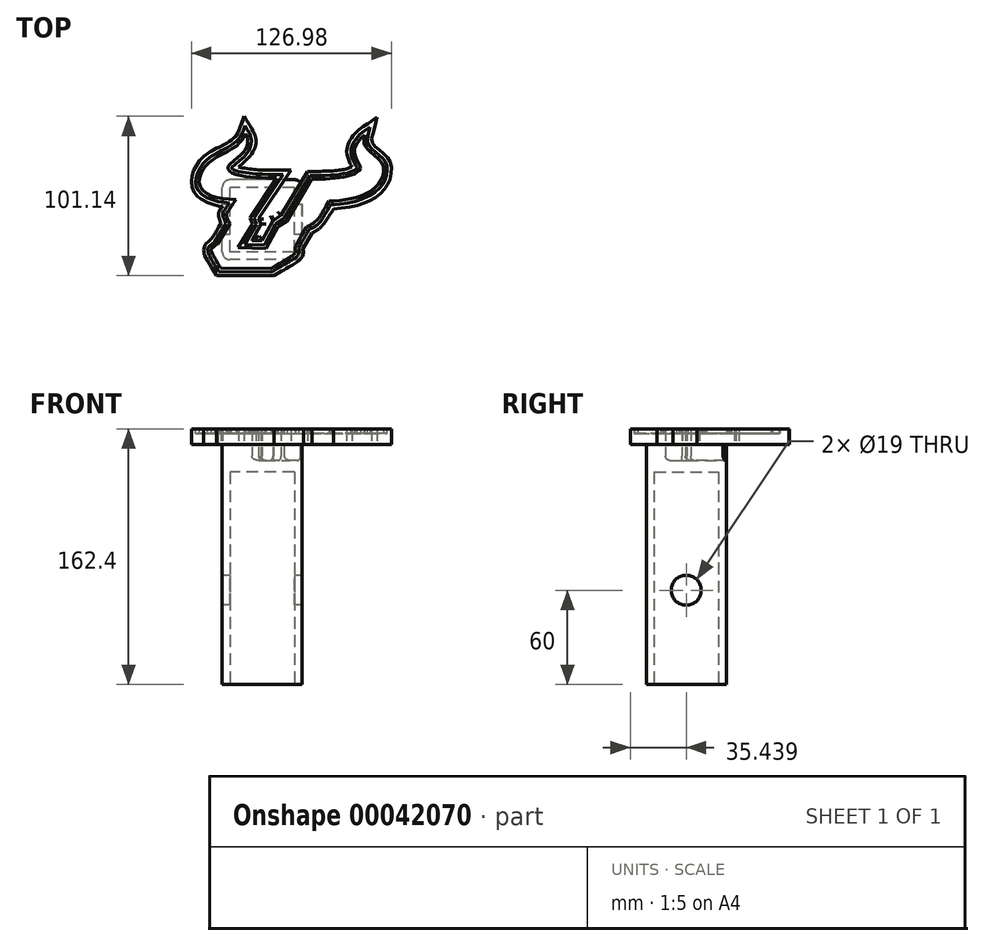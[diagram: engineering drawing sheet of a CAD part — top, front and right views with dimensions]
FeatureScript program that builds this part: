
annotation { "Feature Type Name" : "Feature", "Feature Type Description" : "" }
export const myFeature = defineFeature(function(context is Context, id is Id, definition is map)
    precondition{}
    {
        {
            var Q0;
            Q0=qCreatedBy(makeId("Top.planeOp"),FACE);
            var sketch = newSketch(context, id + "F0", { "sketchPlane" : qUnion([Q0])});
            skFitSpline(sketch, "E0", {"points": [v(-30.7, 0) * mm, v(-32.33, -4.67) * mm, v(-34.46, -10.08) * mm, v(-36.43, -13.03) * mm, v(-39.21, -15.48) * mm, v(-46.09, -19.42) * mm, v(-51.33, -22.04) * mm, v(-57.23, -26.46) * mm, v(-60.67, -30.72) * mm, v(-63.29, -35.96) * mm, v(-64.1, -40.87) * mm, v(-63.62, -45.62) * mm, v(-61.32, -50.04) * mm, v(-57.55, -53) * mm, v(-51.82, -55.45) * mm, v(-46.9, -56.92) * mm, v(-44.45, -57.42) * mm], "startDerivative": vector(-25.69, -73.33) * mm, "endDerivative": vector(51.93, -9.1) * mm});
            skFitSpline(sketch, "E1", {"points": [v(-45.41, -67.95) * mm, v(-46.66, -64.45) * mm, v(-46.9, -62.2) * mm, v(-46.48, -60.18) * mm, v(-44.45, -57.42) * mm], "startDerivative": vector(-5.18, 12.79) * mm, "endDerivative": vector(8.81, 10.21) * mm});
            skFitSpline(sketch, "E2", {"points": [v(-45.41, -67.95) * mm, v(-51.3, -77.63) * mm, v(-52.36, -78.64) * mm, v(-54.44, -80.66) * mm, v(-55.39, -81.67) * mm, v(-56.1, -83.15) * mm, v(-56.28, -86.06) * mm, v(-55.27, -89.44) * mm, v(-48.15, -101.14) * mm], "startDerivative": vector(-33.88, -59.15) * mm, "endDerivative": vector(37.77, -58.28) * mm});
            skFitSpline(sketch, "E3", {"points": [v(-48.15, -101.14) * mm, v(-11.53, -101.14) * mm], "startDerivative": vector(36.62, 0) * mm, "endDerivative": vector(36.62, 0) * mm});
            skFitSpline(sketch, "E4", {"points": [v(-11.53, -101.14) * mm, v(0.85, -93.86) * mm, v(4.9, -90.92) * mm, v(6.8, -87.77) * mm, v(6.74, -84.18) * mm], "startDerivative": vector(36.38, 21.09) * mm, "endDerivative": vector(-2.56, 19.04) * mm});
            skFitSpline(sketch, "E5", {"points": [v(6.74, -84.18) * mm, v(12.58, -74.1) * mm], "startDerivative": vector(5.84, 10.08) * mm, "endDerivative": vector(5.84, 10.08) * mm});
            skFitSpline(sketch, "E6", {"points": [v(12.58, -74.1) * mm, v(15.58, -72.35) * mm, v(19.02, -69.4) * mm, v(26.06, -58.87) * mm], "startDerivative": vector(12.25, 6.8) * mm, "endDerivative": vector(15.82, 25.96) * mm});
            skFitSpline(sketch, "E7", {"points": [v(26.06, -58.87) * mm, v(33, -58.08) * mm, v(33.75, -58.03) * mm, v(39.94, -56.83) * mm, v(48.02, -54.03) * mm, v(53.66, -50.94) * mm, v(57.86, -47.04) * mm, v(60.7, -42.9) * mm, v(62.45, -37.86) * mm, v(62.7, -31.22) * mm, v(61.2, -27.28) * mm, v(58.11, -23.73) * mm, v(53.82, -20.4) * mm, v(51.77, -18.3) * mm, v(50.38, -15.15) * mm, v(51.02, -11.6) * mm, v(53.82, -0.42) * mm], "startDerivative": vector(123.14, 15.03) * mm, "endDerivative": vector(32.52, 137.34) * mm});
            skFitSpline(sketch, "E8", {"points": [v(53.82, -0.42) * mm, v(46.53, -5.52) * mm, v(42.94, -8.11) * mm, v(39.04, -11.66) * mm, v(36.45, -15.5) * mm, v(34.95, -18.94) * mm, v(34.55, -23.34) * mm, v(36.35, -29.57) * mm, v(37.9, -32.12) * mm], "startDerivative": vector(-47.84, -33.44) * mm, "endDerivative": vector(15.88, -22.17) * mm});
            skFitSpline(sketch, "E9", {"points": [v(37.9, -32.12) * mm, v(35.85, -32.97) * mm, v(31.8, -33.97) * mm, v(26.41, -34.62) * mm, v(16.63, -35.02) * mm, v(9.44, -35.12) * mm], "startDerivative": vector(-14.51, -6.75) * mm, "endDerivative": vector(-29.29, -0.26) * mm});
            skFitSpline(sketch, "E10", {"points": [v(9.44, -35.12) * mm, v(-7.16, -62.85) * mm], "startDerivative": vector(-16.6, -27.73) * mm, "endDerivative": vector(-16.6, -27.73) * mm});
            skFitSpline(sketch, "E11", {"points": [v(-7.16, -62.85) * mm, v(-11.95, -66.25) * mm], "startDerivative": vector(-4.8, -3.4) * mm, "endDerivative": vector(-4.8, -3.4) * mm});
            skFitSpline(sketch, "E12", {"points": [v(-11.95, -66.25) * mm, v(-12.39, -66.25) * mm], "startDerivative": vector(-0.44, 0) * mm, "endDerivative": vector(-0.44, 0) * mm});
            skFitSpline(sketch, "E13", {"points": [v(-19.16, -78.81) * mm, v(-25.82, -78.81) * mm], "startDerivative": vector(-6.66, 0) * mm, "endDerivative": vector(-6.66, 0) * mm});
            skFitSpline(sketch, "E14", {"points": [v(-25.82, -78.81) * mm, v(-19.95, -68.31) * mm], "startDerivative": vector(5.86, 10.5) * mm, "endDerivative": vector(5.86, 10.5) * mm});
            skFitSpline(sketch, "E15", {"points": [v(-19.95, -68.31) * mm, v(-21.38, -65.1) * mm], "startDerivative": vector(-1.43, 3.2) * mm, "endDerivative": vector(-1.43, 3.2) * mm});
            skFitSpline(sketch, "E16", {"points": [v(-21.38, -65.1) * mm, v(-0.87, -34.23) * mm], "startDerivative": vector(20.5, 30.87) * mm, "endDerivative": vector(20.5, 30.87) * mm});
            skFitSpline(sketch, "E17", {"points": [v(-0.87, -34.23) * mm, v(-12.32, -34.23) * mm, v(-23.7, -33.86) * mm, v(-34.36, -32.32) * mm], "startDerivative": vector(-33.9, -0.05) * mm, "endDerivative": vector(-32.28, 5.6) * mm});
            skFitSpline(sketch, "E18", {"points": [v(-34.36, -32.32) * mm, v(-30.27, -28.8) * mm, v(-26.07, -24.04) * mm, v(-23.78, -19.68) * mm, v(-23.14, -16.55) * mm, v(-23.58, -13.02) * mm, v(-25.52, -8.55) * mm, v(-30.7, 0) * mm], "startDerivative": vector(28.11, 23.08) * mm, "endDerivative": vector(-29.43, 46.8) * mm});
            skLineSegment(sketch, "E19", {"start": v(-19.16, -78.81) * mm, "end": v(-12.39, -66.25) * mm});
            skFitSpline(sketch, "E20", {"points": [v(-29.86, -11) * mm, v(-30.67, -12.93) * mm, v(-31.74, -14.72) * mm, v(-33.53, -16.91) * mm, v(-36.44, -19.42) * mm, v(-40.83, -22.1) * mm, v(-45.3, -24.48) * mm, v(-50.46, -27.39) * mm, v(-53.41, -29.76) * mm, v(-55.83, -32.36) * mm, v(-57.76, -35.85) * mm, v(-58.97, -39.66) * mm, v(-59.01, -43.15) * mm, v(-57.44, -46.55) * mm, v(-54.09, -49.24) * mm, v(-49.43, -51.25) * mm, v(-44.06, -52.33) * mm, v(-35.96, -53) * mm], "startDerivative": vector(-18.17, -47.16) * mm, "endDerivative": vector(103.54, -6.88) * mm});
            skFitSpline(sketch, "E21", {"points": [v(-35.96, -53) * mm, v(-41.07, -60.57) * mm, v(-41.71, -61.5) * mm, v(-41.91, -61.86) * mm, v(-42, -62.29) * mm, v(-41.91, -63.1) * mm, v(-41.3, -65) * mm, v(-39.71, -68.27) * mm], "startDerivative": vector(-19.95, -29.75) * mm, "endDerivative": vector(8.84, -17.26) * mm});
            skFitSpline(sketch, "E22", {"points": [v(-39.71, -68.27) * mm, v(-47.67, -81.04) * mm], "startDerivative": vector(-7.95, -12.78) * mm, "endDerivative": vector(-7.95, -12.78) * mm});
            skFitSpline(sketch, "E23", {"points": [v(-47.67, -81.04) * mm, v(-50.91, -83.72) * mm, v(-51.33, -84.14) * mm, v(-51.56, -84.85) * mm, v(-51.17, -86.51) * mm, v(-45.64, -96.33) * mm], "startDerivative": vector(-16.29, -13.47) * mm, "endDerivative": vector(17.45, -29.26) * mm});
            skFitSpline(sketch, "E24", {"points": [v(-45.64, -96.33) * mm, v(-13.5, -96.69) * mm], "startDerivative": vector(32.13, -0.36) * mm, "endDerivative": vector(32.13, -0.36) * mm});
            skFitSpline(sketch, "E25", {"points": [v(-13.5, -96.69) * mm, v(-1.14, -89.27) * mm, v(0, -88.47) * mm, v(1.29, -87.43) * mm, v(1.89, -86.68) * mm, v(1.97, -85.96) * mm, v(1.65, -83.48) * mm, v(1.65, -83.2) * mm, v(1.93, -82.65) * mm, v(8.99, -70.16) * mm], "startDerivative": vector(61.62, 36.5) * mm, "endDerivative": vector(36.44, 64.3) * mm});
            skFitSpline(sketch, "E26", {"points": [v(8.99, -70.16) * mm, v(10.15, -69.83) * mm, v(12.08, -68.68) * mm, v(14.38, -67) * mm, v(16, -65.48) * mm, v(16.49, -65.03) * mm, v(17.38, -63.58) * mm, v(18.97, -61.03) * mm, v(23.25, -53.93) * mm], "startDerivative": vector(12.63, 2.66) * mm, "endDerivative": vector(20.71, 34.76) * mm});
            skFitSpline(sketch, "E27", {"points": [v(23.25, -53.93) * mm, v(25.7, -53.84) * mm, v(31.14, -53.38) * mm, v(34.72, -52.84) * mm, v(38.45, -52.09) * mm, v(41.5, -51.21) * mm, v(44.44, -50.17) * mm, v(47.39, -48.82) * mm, v(51.04, -46.54) * mm, v(54.07, -43.73) * mm, v(55.95, -41.06) * mm, v(57.1, -38.7) * mm, v(57.78, -35.97) * mm, v(57.94, -33.56) * mm, v(57.66, -31.69) * mm, v(56.5, -29.25) * mm, v(54, -26.5) * mm, v(50.66, -23.79) * mm, v(48.93, -22.35) * mm, v(47.87, -21.32) * mm, v(46.87, -20) * mm, v(45.92, -18.2) * mm, v(45.48, -16.21) * mm, v(45.48, -14.12) * mm, v(45.92, -11.84) * mm], "startDerivative": vector(55.72, 1.37) * mm, "endDerivative": vector(14.32, 61.27) * mm});
            skFitSpline(sketch, "E28", {"points": [v(45.92, -11.84) * mm, v(44.08, -13.44) * mm, v(42.4, -15.25) * mm, v(41.23, -16.77) * mm, v(40.1, -18.88) * mm, v(39.55, -20.74) * mm, v(39.41, -22.23) * mm, v(39.5, -23.61) * mm, v(39.85, -25.19) * mm, v(40.6, -26.98) * mm, v(41.59, -28.92) * mm, v(42.52, -30.57) * mm, v(43, -31.87) * mm, v(43.12, -32.62) * mm, v(42.9, -33.66) * mm, v(42.29, -34.56) * mm, v(41.55, -35.26) * mm, v(40.51, -35.93) * mm, v(39.31, -36.63) * mm, v(37.5, -37.27) * mm, v(35.34, -37.99) * mm, v(32.91, -38.55) * mm, v(30.26, -38.95) * mm, v(27.1, -39.35) * mm, v(23.42, -39.74) * mm, v(19.85, -39.92) * mm, v(12.3, -40.02) * mm], "startDerivative": vector(-44.36, -36.44) * mm, "endDerivative": vector(-112.65, -1) * mm});
            skFitSpline(sketch, "E29", {"points": [v(12.3, -40.02) * mm, v(-3.52, -66.47) * mm], "startDerivative": vector(-15.8, -26.45) * mm, "endDerivative": vector(-15.8, -26.45) * mm});
            skFitSpline(sketch, "E30", {"points": [v(-3.52, -66.47) * mm, v(-9.11, -69.93) * mm], "startDerivative": vector(-5.6, -3.46) * mm, "endDerivative": vector(-5.6, -3.46) * mm});
            skFitSpline(sketch, "E31", {"points": [v(-9.11, -69.93) * mm, v(-16.66, -83.93) * mm], "startDerivative": vector(-7.54, -14) * mm, "endDerivative": vector(-7.54, -14) * mm});
            skFitSpline(sketch, "E32", {"points": [v(-16.66, -83.93) * mm, v(-34.47, -83.53) * mm], "startDerivative": vector(-17.82, 0.4) * mm, "endDerivative": vector(-17.82, 0.4) * mm});
            skFitSpline(sketch, "E33", {"points": [v(-34.47, -83.53) * mm, v(-25.2, -68.6) * mm], "startDerivative": vector(9.28, 14.92) * mm, "endDerivative": vector(9.28, 14.92) * mm});
            skFitSpline(sketch, "E34", {"points": [v(-25.2, -68.6) * mm, v(-27.07, -64.7) * mm], "startDerivative": vector(-1.87, 3.9) * mm, "endDerivative": vector(-1.87, 3.9) * mm});
            skFitSpline(sketch, "E35", {"points": [v(-27.07, -64.7) * mm, v(-10.2, -39.2) * mm], "startDerivative": vector(16.86, 25.5) * mm, "endDerivative": vector(16.86, 25.5) * mm});
            skFitSpline(sketch, "E36", {"points": [v(-10.2, -39.2) * mm, v(-14.94, -39.2) * mm, v(-20.77, -38.95) * mm, v(-26.27, -38.62) * mm, v(-30.9, -38) * mm, v(-35.44, -36.98) * mm, v(-38.82, -35.73) * mm, v(-40.43, -34.41) * mm, v(-40.9, -33.43) * mm, v(-40.97, -32.5) * mm, v(-40.46, -31.45) * mm, v(-37.14, -28.35) * mm, v(-33.97, -25.66) * mm, v(-32, -23.77) * mm, v(-30.24, -21.6) * mm, v(-28.86, -19.02) * mm, v(-28.39, -16.96) * mm, v(-28.42, -14.84) * mm, v(-28.9, -12.87) * mm, v(-29.86, -11) * mm], "startDerivative": vector(-69.13, -0.84) * mm, "endDerivative": vector(-24.17, 41.39) * mm});
            skFitSpline(sketch, "E37", {"points": [v(-30.18, -6.06) * mm, v(-31.32, -9.14) * mm, v(-32.46, -11.76) * mm, v(-34.32, -14.55) * mm, v(-37.24, -17.21) * mm, v(-40.79, -19.66) * mm, v(-46.37, -22.54) * mm, v(-50.68, -24.99) * mm, v(-54.82, -27.99) * mm, v(-57.7, -31.16) * mm, v(-60.1, -35.68) * mm, v(-61.29, -39.4) * mm, v(-61.5, -42.02) * mm, v(-60.95, -45.1) * mm, v(-59.6, -47.55) * mm, v(-55.8, -50.8) * mm, v(-50.56, -53.22) * mm, v(-45.19, -54.4) * mm, v(-40.03, -55.07) * mm], "startDerivative": vector(-23.44, -64.55) * mm, "endDerivative": vector(83.33, -9.9) * mm});
            skFitSpline(sketch, "E38", {"points": [v(-40.03, -55.07) * mm, v(-43, -59.43) * mm, v(-43.96, -60.9) * mm, v(-44.22, -62.64) * mm, v(-43.88, -64.37) * mm, v(-42.15, -68.17) * mm], "startDerivative": vector(-11.94, -18.13) * mm, "endDerivative": vector(8.4, -17.03) * mm});
            skFitSpline(sketch, "E39", {"points": [v(-42.15, -68.17) * mm, v(-49.6, -79.9) * mm], "startDerivative": vector(-7.45, -11.73) * mm, "endDerivative": vector(-7.45, -11.73) * mm});
            skFitSpline(sketch, "E40", {"points": [v(-49.6, -79.9) * mm, v(-51.71, -81.74) * mm, v(-52.83, -82.66) * mm, v(-53.39, -83.25) * mm, v(-53.79, -84.21) * mm, v(-53.75, -85.33) * mm, v(-53.35, -86.96) * mm, v(-51.87, -90.31) * mm, v(-46.85, -98.61) * mm], "startDerivative": vector(-16.34, -14.43) * mm, "endDerivative": vector(22.5, -35.56) * mm});
            skFitSpline(sketch, "E41", {"points": [v(-46.85, -98.61) * mm, v(-12.9, -98.93) * mm], "startDerivative": vector(33.94, -0.32) * mm, "endDerivative": vector(33.94, -0.32) * mm});
            skFitSpline(sketch, "E42", {"points": [v(-12.9, -98.93) * mm, v(-0.28, -91.28) * mm, v(1.46, -90.2) * mm, v(2.54, -89.3) * mm, v(3.42, -88.34) * mm, v(4.02, -87.26) * mm, v(4.2, -86.43) * mm, v(3.92, -83.67) * mm], "startDerivative": vector(45.69, 27.8) * mm, "endDerivative": vector(-2.95, 21.72) * mm});
            skFitSpline(sketch, "E43", {"points": [v(3.92, -83.67) * mm, v(7.86, -76.76) * mm, v(10.55, -71.96) * mm], "startDerivative": vector(7.55, 13.23) * mm, "endDerivative": vector(5.64, 10.1) * mm});
            skFitSpline(sketch, "E44", {"points": [v(10.55, -71.96) * mm, v(11.59, -71.53) * mm, v(13.2, -70.57) * mm, v(15.15, -69.36) * mm, v(17.88, -66.8) * mm, v(20.02, -63.44) * mm, v(24.5, -56.13) * mm], "startDerivative": vector(10.1, 3.69) * mm, "endDerivative": vector(18.45, 29.55) * mm});
            skFitSpline(sketch, "E45", {"points": [v(24.5, -56.13) * mm, v(26.06, -56.13) * mm, v(28.87, -55.84) * mm, v(33.5, -55.26) * mm, v(39.29, -54.15) * mm, v(45.4, -52.18) * mm, v(51.21, -49.1) * mm, v(54.42, -46.5) * mm, v(56.7, -44.04) * mm, v(58.2, -41.79) * mm, v(59.21, -39.31) * mm, v(59.95, -36.7) * mm, v(60.14, -34.6) * mm, v(60.05, -32.38) * mm, v(59.6, -30.6) * mm, v(58.84, -28.8) * mm, v(57.57, -27.05) * mm, v(55.56, -24.96) * mm, v(53.7, -23.44) * mm, v(51.75, -21.92) * mm, v(50.06, -20.4) * mm, v(49, -19.29) * mm, v(48.16, -17.9) * mm, v(47.63, -16.01) * mm, v(47.63, -14.2) * mm, v(48.37, -10.86) * mm, v(49.39, -6.81) * mm], "startDerivative": vector(51.65, -1.58) * mm, "endDerivative": vector(22.14, 87.59) * mm});
            skFitSpline(sketch, "E46", {"points": [v(49.39, -6.81) * mm, v(45.9, -9.14) * mm, v(43.74, -10.8) * mm, v(42.01, -12.45) * mm, v(40.18, -14.5) * mm, v(38.79, -16.57) * mm, v(37.77, -19.02) * mm, v(37.25, -21.74) * mm, v(37.4, -24.15) * mm, v(38.1, -26.72) * mm, v(39.76, -30.18) * mm, v(40.6, -31.81) * mm, v(40.9, -32.38) * mm, v(41, -32.73) * mm, v(40.88, -33.07) * mm, v(40.27, -33.68) * mm, v(39.58, -34.19) * mm, v(38.6, -34.71) * mm, v(37.28, -35.21) * mm, v(35.51, -35.83) * mm, v(32.63, -36.45) * mm, v(30.28, -36.83) * mm, v(27.3, -37.18) * mm, v(24.75, -37.37) * mm, v(19.78, -37.7) * mm, v(11.07, -37.79) * mm], "startDerivative": vector(-67.65, -44.18) * mm, "endDerivative": vector(-116.52, 0.6) * mm});
            skFitSpline(sketch, "E47", {"points": [v(11.07, -37.79) * mm, v(-5.3, -64.88) * mm], "startDerivative": vector(-16.36, -27.1) * mm, "endDerivative": vector(-16.36, -27.1) * mm});
            skFitSpline(sketch, "E48", {"points": [v(-5.3, -64.88) * mm, v(-10.88, -68.54) * mm], "startDerivative": vector(-5.59, -3.66) * mm, "endDerivative": vector(-5.59, -3.66) * mm});
            skFitSpline(sketch, "E49", {"points": [v(-10.88, -68.54) * mm, v(-17.88, -81.67) * mm], "startDerivative": vector(-7, -13.13) * mm, "endDerivative": vector(-7, -13.13) * mm});
            skFitSpline(sketch, "E50", {"points": [v(-17.88, -81.67) * mm, v(-30.49, -81.39) * mm], "startDerivative": vector(-12.6, 0.28) * mm, "endDerivative": vector(-12.6, 0.28) * mm});
            skFitSpline(sketch, "E51", {"points": [v(-30.49, -81.39) * mm, v(-22.72, -68.38) * mm], "startDerivative": vector(7.76, 13) * mm, "endDerivative": vector(7.76, 13) * mm});
            skFitSpline(sketch, "E52", {"points": [v(-22.72, -68.38) * mm, v(-24.52, -64.8) * mm], "startDerivative": vector(-1.8, 3.59) * mm, "endDerivative": vector(-1.8, 3.59) * mm});
            skFitSpline(sketch, "E53", {"points": [v(-24.52, -64.8) * mm, v(-5.92, -37.02) * mm], "startDerivative": vector(18.6, 27.78) * mm, "endDerivative": vector(18.6, 27.78) * mm});
            skFitSpline(sketch, "E54", {"points": [v(-5.92, -37.02) * mm, v(-10.49, -37.02) * mm, v(-12.61, -37.02) * mm, v(-16.25, -36.9) * mm, v(-21.94, -36.64) * mm, v(-29.23, -35.92) * mm, v(-33.9, -35.2) * mm, v(-34.13, -35.18) * mm, v(-36.88, -34.32) * mm, v(-38.07, -33.73) * mm, v(-38.6, -33.19) * mm, v(-38.74, -32.87) * mm, v(-38.55, -32.47) * mm, v(-37.4, -31.45) * mm, v(-33.15, -28) * mm, v(-30.15, -25.07) * mm, v(-28.65, -23.25) * mm, v(-27.59, -21.53) * mm, v(-26.92, -20.1) * mm, v(-26.43, -18.53) * mm, v(-26.08, -16.63) * mm, v(-26.2, -14.6) * mm, v(-26.67, -12.42) * mm, v(-27.38, -10.77) * mm, v(-28.95, -8.14) * mm, v(-30.18, -6.06) * mm], "startDerivative": vector(-90.9, 0.18) * mm, "endDerivative": vector(-28.37, 48.8) * mm});
            skSolve(sketch);
        }
        {
            var Q0;
            Q0=makeQuery(id+"F0.imprint","IMPRINT",FACE,{"disambiguationData":[TD([[makeQuery(id+"F0.imprint","IMPRINT",EDGE,{"derivedFrom":sQuery(id+"F0.wireOp",EDGE,"E20")}),-1.0]])]});
            var Q1;
            Q1=makeQuery(id+"F0.imprint","IMPRINT",FACE,{"disambiguationData":[TD([[makeQuery(id+"F0.imprint","IMPRINT",EDGE,{"derivedFrom":sQuery(id+"F0.wireOp",EDGE,"E0")}),1.0]])]});
            var Q2;
            Q2=makeQuery(id+"F0.imprint","IMPRINT",FACE,{"disambiguationData":[TD([[makeQuery(id+"F0.imprint","IMPRINT",EDGE,{"derivedFrom":sQuery(id+"F0.wireOp",EDGE,"E20")}),1.0]])]});
            extrude(context, id + "F1", {"entities" : qUnion([Q0, Q1, Q2]), "depth" : 7 * mm});
        }
        {
            var Q0;
            Q0=makeQuery(id+"F0.imprint","IMPRINT",FACE,{"disambiguationData":[TD([[makeQuery(id+"F0.imprint","IMPRINT",EDGE,{"derivedFrom":sQuery(id+"F0.wireOp",EDGE,"E20")}),1.0]])]});
            var Q1;
            Q1=makeQuery(id+"F0.imprint","IMPRINT",FACE,{"disambiguationData":[TD([[makeQuery(id+"F0.imprint","IMPRINT",EDGE,{"derivedFrom":sQuery(id+"F0.wireOp",EDGE,"E0")}),1.0]])]});
            extrude(context, id + "F2", {"entities" : qUnion([Q0, Q1]), "operationType" : NewBodyOperationType.ADD, "depth" : 10 * mm});
        }
        {
            var Q0;
            Q0=qCreatedBy(makeId("Top.planeOp"),FACE);
            var sketch = newSketch(context, id + "F3", { "sketchPlane" : qUnion([Q0])});
            skLineSegment(sketch, "E55.rect.bottom", {"start": v(1.24, -91.1) * mm, "end": v(-39.56, -91.1) * mm});
            skLineSegment(sketch, "E55.rect.top", {"start": v(1.24, -40.3) * mm, "end": v(-39.56, -40.3) * mm});
            skLineSegment(sketch, "E55.rect.left", {"start": v(6.24, -86.1) * mm, "end": v(6.24, -45.3) * mm});
            skLineSegment(sketch, "E55.rect.right", {"start": v(-44.56, -86.1) * mm, "end": v(-44.56, -45.3) * mm});
            skPoint(sketch, "E55.rect.middle", {"position": v(-19.16, -65.7) * mm});
            skPoint(sketch, "E56.visualSharp", {"position": v(-44.56, -91.1) * mm});
            skArc(sketch, "E56.filletArc", {"start": v(-44.56, -86.1) * mm, "mid": v(-43.1, -89.64) * mm, "end": v(-39.56, -91.1) * mm});
            skPoint(sketch, "E57.visualSharp", {"position": v(6.24, -91.1) * mm});
            skArc(sketch, "E57.filletArc", {"start": v(1.24, -91.1) * mm, "mid": v(4.77, -89.64) * mm, "end": v(6.24, -86.1) * mm});
            skPoint(sketch, "E58.visualSharp", {"position": v(6.24, -40.3) * mm});
            skArc(sketch, "E58.filletArc", {"start": v(6.24, -45.3) * mm, "mid": v(4.77, -41.77) * mm, "end": v(1.24, -40.3) * mm});
            skPoint(sketch, "E59.visualSharp", {"position": v(-44.56, -40.3) * mm});
            skArc(sketch, "E59.filletArc", {"start": v(-39.56, -40.3) * mm, "mid": v(-43.1, -41.77) * mm, "end": v(-44.56, -45.3) * mm});
            skSolve(sketch);
        }
        {
            var Q0;
            Q0 = qSketchRegion(id + "F3", true);
            extrude(context, id + "F4", {"entities" : qUnion([Q0]), "operationType" : NewBodyOperationType.ADD, "oppositeDirection" : true, "depth" : 152.4 * mm});
        }
        {
            var Q0;
            {var subQ0=sQuery(id+"F3.wireOp",EDGE,"E55.rect.top");var subQ1=sQuery(id+"F3.wireOp",EDGE,"E58.filletArc");var subQ8=sQuery(id+"F0.wireOp",EDGE,"E10");Q0=makeQuery(id+"F4.boolean.opBoolean","SPLIT",FACE,{"disambiguationData":[TD([makeQuery(id+"F1.opExtrude","SWEPT_FACE",FACE,{"disambiguationData":[OSD([subQ8])]})])],"derivedFrom":makeQuery(id+"F4.opExtrude","CAP_FACE",FACE,{"disambiguationData":[OSD([sQuery(id+"F3.wireOp",EDGE,"E55.rect.bottom"),subQ0,sQuery(id+"F3.wireOp",EDGE,"E55.rect.left"),sQuery(id+"F3.wireOp",EDGE,"E55.rect.right"),sQuery(id+"F3.wireOp",EDGE,"E56.filletArc"),sQuery(id+"F3.wireOp",EDGE,"E57.filletArc"),subQ1,sQuery(id+"F3.wireOp",EDGE,"E59.filletArc")])],"isStart":true})});}
            extrude(context, id + "F5", {"entities" : qUnion([Q0]), "operationType" : NewBodyOperationType.REMOVE, "oppositeDirection" : true, "depth" : 10 * mm});
        }
        {
            var Q0;
            Q0=makeQuery(id+"F5.boolean.opBoolean","COPY",EDGE,{"derivedFrom":makeQuery(id+"F5.opExtrude","CAP_EDGE",EDGE,{"disambiguationData":[OSD([sQuery(id+"F0.wireOp",EDGE,"E16")])],"isStart":false})});
            var Q1;
            Q1=makeQuery(id+"F5.boolean.opBoolean","COPY",EDGE,{"derivedFrom":makeQuery(id+"F5.opExtrude","CAP_EDGE",EDGE,{"disambiguationData":[OSD([sQuery(id+"F0.wireOp",EDGE,"E15")])],"isStart":false})});
            var Q2;
            Q2=makeQuery(id+"F5.boolean.opBoolean","COPY",EDGE,{"derivedFrom":makeQuery(id+"F5.opExtrude","CAP_EDGE",EDGE,{"disambiguationData":[OSD([sQuery(id+"F0.wireOp",EDGE,"E14")])],"isStart":false})});
            var Q3;
            Q3=makeQuery(id+"F5.boolean.opBoolean","COPY",EDGE,{"derivedFrom":makeQuery(id+"F5.opExtrude","CAP_EDGE",EDGE,{"disambiguationData":[OSD([sQuery(id+"F0.wireOp",EDGE,"E13")])],"isStart":false})});
            var Q4;
            Q4=makeQuery(id+"F5.boolean.opBoolean","COPY",EDGE,{"derivedFrom":makeQuery(id+"F5.opExtrude","CAP_EDGE",EDGE,{"disambiguationData":[OSD([sQuery(id+"F0.wireOp",EDGE,"E10")])],"isStart":false})});
            var Q5;
            Q5=makeQuery(id+"F5.boolean.opBoolean","COPY",EDGE,{"derivedFrom":makeQuery(id+"F5.opExtrude","CAP_EDGE",EDGE,{"disambiguationData":[OSD([sQuery(id+"F0.wireOp",EDGE,"E11")])],"isStart":false})});
            var Q6;
            Q6=makeQuery(id+"F5.boolean.opBoolean","COPY",EDGE,{"derivedFrom":makeQuery(id+"F5.opExtrude","CAP_EDGE",EDGE,{"disambiguationData":[OSD([sQuery(id+"F0.wireOp",EDGE,"E12")])],"isStart":false})});
            var Q7;
            Q7=makeQuery(id+"F5.boolean.opBoolean","COPY",EDGE,{"derivedFrom":makeQuery(id+"F5.opExtrude","CAP_EDGE",EDGE,{"disambiguationData":[OSD([sQuery(id+"F0.wireOp",EDGE,"E19")])],"isStart":false})});
            fillet(context, id + "F6", {"entities" : qUnion([Q0, Q1, Q2, Q3, Q4, Q5, Q6, Q7]), "radius" : 2.75 * mm, "tangentPropagation" : true, "allowEdgeOverflow" : false});
        }
        {
            var Q0;
            Q0=makeQuery(id+"F4.opExtrude","CAP_FACE",FACE,{"disambiguationData":[OSD([sQuery(id+"F3.wireOp",EDGE,"E55.rect.bottom"),sQuery(id+"F3.wireOp",EDGE,"E55.rect.top"),sQuery(id+"F3.wireOp",EDGE,"E55.rect.left"),sQuery(id+"F3.wireOp",EDGE,"E55.rect.right"),sQuery(id+"F3.wireOp",EDGE,"E56.filletArc"),sQuery(id+"F3.wireOp",EDGE,"E57.filletArc"),sQuery(id+"F3.wireOp",EDGE,"E58.filletArc"),sQuery(id+"F3.wireOp",EDGE,"E59.filletArc")])],"isStart":false});
            var sketch = newSketch(context, id + "F7", { "sketchPlane" : qUnion([Q0])});
            skLineSegment(sketch, "E60.0", {"start": v(1.24, 45.3) * mm, "end": v(-39.56, 45.3) * mm});
            skLineSegment(sketch, "E60.1", {"start": v(1.24, 86.1) * mm, "end": v(1.24, 45.3) * mm});
            skLineSegment(sketch, "E60.2", {"start": v(1.24, 86.1) * mm, "end": v(-39.56, 86.1) * mm});
            skLineSegment(sketch, "E60.3", {"start": v(-39.56, 86.1) * mm, "end": v(-39.56, 45.3) * mm});
            skSolve(sketch);
        }
        {
            var Q0;
            Q0=makeQuery(id+"F7.imprint","IMPRINT",FACE,{"disambiguationData":[TD([[makeQuery(id+"F7.imprint","IMPRINT",EDGE,{"derivedFrom":sQuery(id+"F7.wireOp",EDGE,"E60.0")}),-1.0]])]});
            extrude(context, id + "F8", {"entities" : qUnion([Q0]), "operationType" : NewBodyOperationType.REMOVE, "oppositeDirection" : true, "depth" : 135 * mm});
        }
        {
            var Q0;
            Q0=makeQuery(id+"F4.opExtrude","SWEPT_FACE",FACE,{"disambiguationData":[OSD([sQuery(id+"F3.wireOp",EDGE,"E55.rect.right")])]});
            var sketch = newSketch(context, id + "F9", { "sketchPlane" : qUnion([Q0])});
            skLineSegment(sketch, "E61", {"start": v(65.7, -152.4) * mm, "end": v(65.7, -92.4) * mm, "construction": true});
            skCircle(sketch, "E62", {"center": v(65.7, -92.4) * mm, "radius": 9.5 * mm});
            skSolve(sketch);
        }
        {
            var Q0;
            Q0 = qSketchRegion(id + "F9", true);
            extrude(context, id + "F10", {"entities" : qUnion([Q0]), "operationType" : NewBodyOperationType.REMOVE, "oppositeDirection" : true, "depth" : 60 * mm});
        }
    });
